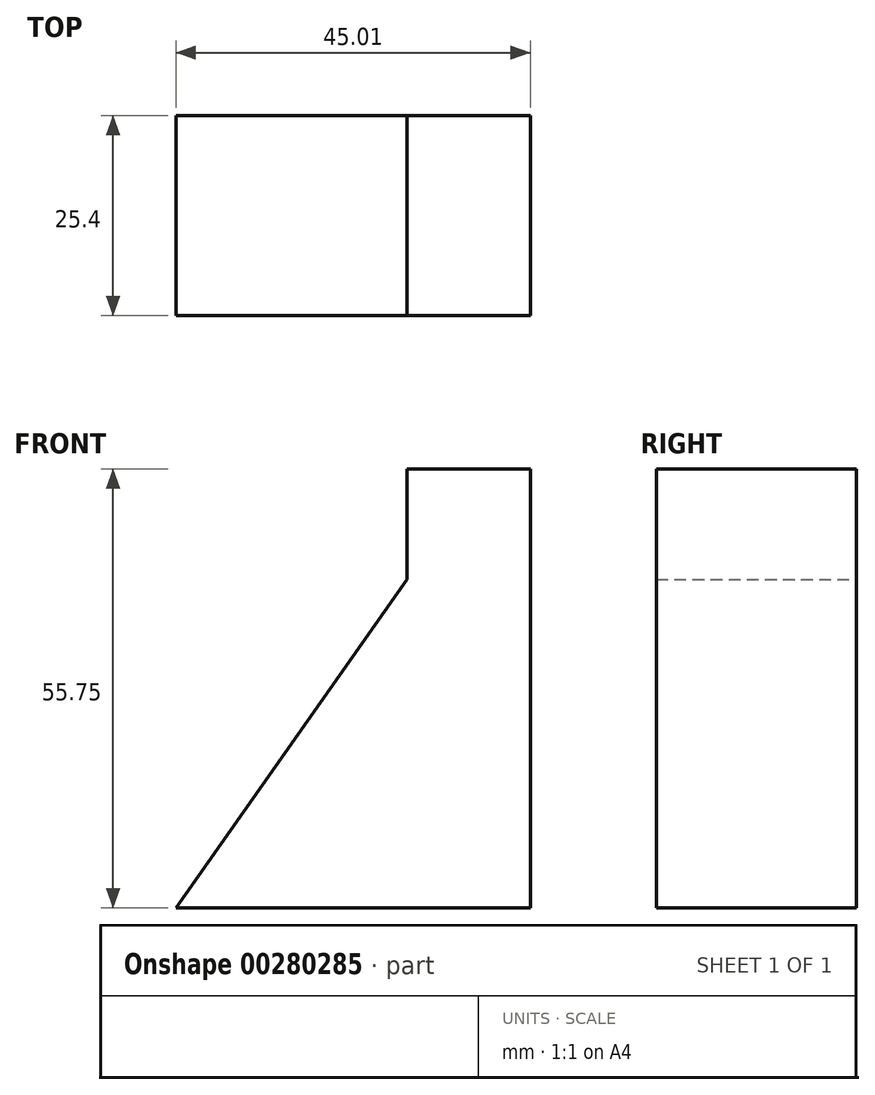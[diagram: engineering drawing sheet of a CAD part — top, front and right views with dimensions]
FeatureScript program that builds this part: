
annotation { "Feature Type Name" : "Feature", "Feature Type Description" : "" }
export const myFeature = defineFeature(function(context is Context, id is Id, definition is map)
    precondition{}
    {
        {
            var Q0;
            Q0=qCreatedBy(makeId("Front.planeOp"),FACE);
            var sketch = newSketch(context, id + "F0", { "sketchPlane" : qUnion([Q0])});
            skLineSegment(sketch, "E0", {"start": v(0, 55.75) * mm, "end": v(-15.64, 55.75) * mm});
            skLineSegment(sketch, "E1", {"start": v(-15.64, 55.75) * mm, "end": v(-15.64, 41.7) * mm});
            skLineSegment(sketch, "E2", {"start": v(0, 55.75) * mm, "end": v(0, -1.5) * mm});
            skLineSegment(sketch, "E3", {"start": v(0, 0) * mm, "end": v(-45, 0) * mm});
            skLineSegment(sketch, "E4", {"start": v(-45, 0) * mm, "end": v(-15.64, 41.7) * mm});
            skSolve(sketch);
        }
        {
            var Q0;
            Q0 = qSketchRegion(id + "F0", true);
            extrude(context, id + "F1", {"entities" : qUnion([Q0]), "depth" : 25.4 * mm});
        }
    });
